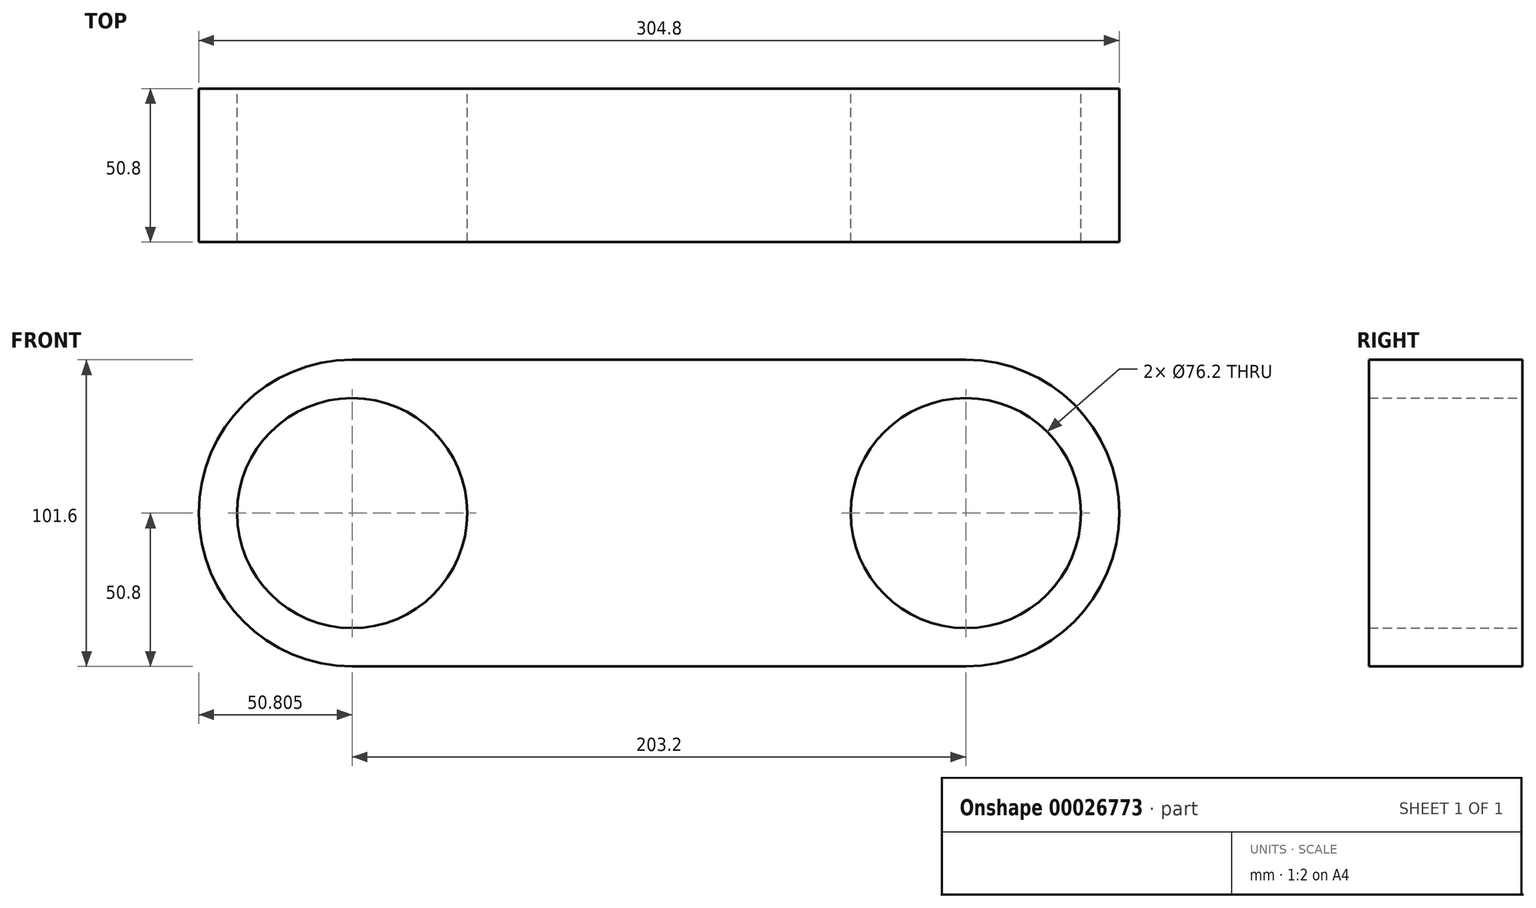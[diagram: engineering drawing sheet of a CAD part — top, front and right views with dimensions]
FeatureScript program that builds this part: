
annotation { "Feature Type Name" : "Feature", "Feature Type Description" : "" }
export const myFeature = defineFeature(function(context is Context, id is Id, definition is map)
    precondition{}
    {
        {
            var Q0;
            Q0=qCreatedBy(makeId("Front.planeOp"),FACE);
            var sketch = newSketch(context, id + "F0", { "sketchPlane" : qUnion([Q0])});
            skLineSegment(sketch, "E0.bottom", {"start": v(-81.25, -50.8) * mm, "end": v(121.95, -50.8) * mm});
            skLineSegment(sketch, "E0.top", {"start": v(-81.25, 50.8) * mm, "end": v(121.95, 50.8) * mm});
            skArc(sketch, "E1", {"start": v(-81.25, 50.8) * mm, "mid": v(-132.05, 0) * mm, "end": v(-81.25, -50.8) * mm});
            skArc(sketch, "E2", {"start": v(121.95, -50.8) * mm, "mid": v(172.75, 0) * mm, "end": v(121.95, 50.8) * mm});
            skCircle(sketch, "E3", {"center": v(-81.25, 0) * mm, "radius": 38.1 * mm});
            skCircle(sketch, "E4", {"center": v(121.95, 0) * mm, "radius": 38.1 * mm});
            skSolve(sketch);
        }
        {
            var Q0;
            Q0=makeQuery(id+"F0.imprint","IMPRINT",FACE,{"disambiguationData":[TD([[makeQuery(id+"F0.imprint","IMPRINT",EDGE,{"derivedFrom":sQuery(id+"F0.wireOp",EDGE,"E0.bottom")}),1.0]])]});
            extrude(context, id + "F1", {"entities" : qUnion([Q0]), "depth" : 50.8 * mm});
        }
    });
